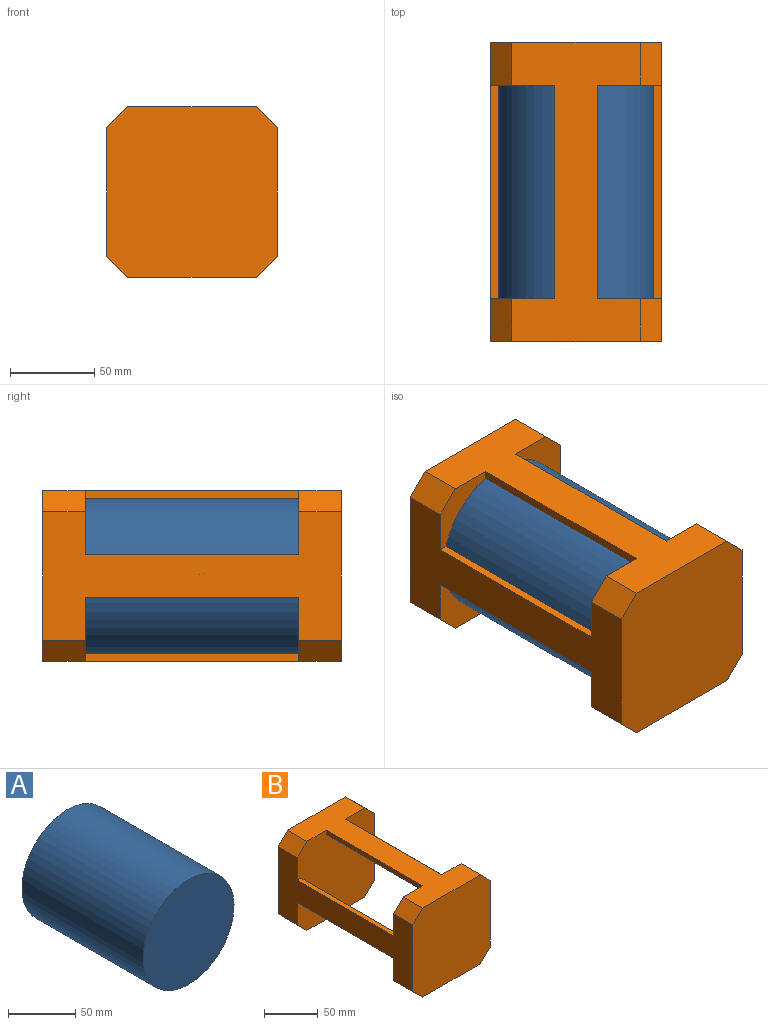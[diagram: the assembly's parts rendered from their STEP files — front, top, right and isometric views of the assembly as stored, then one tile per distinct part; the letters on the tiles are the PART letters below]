
ASSEMBLY  parts=2 mates=1
PART A: 3 faces, bbox 95.3x127x95.3 mm
  f0: cylinder r=47.62mm len=127mm, axis (0,-1,0), area 38003.1mm2, adj f1,f2
  f1: plane 95.25x95.25mm, normal (0,1,0), area 7125.6mm2, adj f0
  f2: plane 95.25x95.25mm, normal (0,-1,0), area 7125.6mm2, adj f0
PART B: 28 faces, bbox 101.6x177.8x101.6 mm
  f0: plane 101.6x101.6mm, normal (0,1,0), area 9619.4mm2, adj f1,f2,f3,f4,f5,f6,f7,f8
  f1: plane 177.8x76.2mm, normal (0,0,-1), area 7096.8mm2, adj f0,f2,f8,f9,f13,f14,f22,f23
  f2: plane 25.4x12.7mm, normal (0.71,0,-0.71), area 456.2mm2, adj f0,f1,f3,f9
  f3: plane 177.8x76.2mm, normal (1,0,0), area 7096.8mm2, adj f0,f2,f4,f9,f19,f21,f22,f23
  f4: plane 25.4x12.7mm, normal (0.71,0,0.71), area 456.2mm2, adj f0,f3,f5,f9
  f5: plane 177.8x76.2mm, normal (0,0,1), area 7096.8mm2, adj f0,f4,f6,f9,f10,f12,f22,f24
  f6: plane 25.4x12.7mm, normal (-0.71,0,0.71), area 456.2mm2, adj f0,f5,f7,f9
  f7: plane 177.8x76.2mm, normal (-1,0,0), area 7096.8mm2, adj f0,f6,f8,f9,f17,f18,f22,f25
  f8: plane 25.4x12.7mm, normal (-0.71,0,-0.71), area 456.2mm2, adj f0,f1,f7,f9
  f9: plane 101.6x101.6mm, normal (0,-1,0), area 10000mm2, adj f1,f2,f3,f4,f5,f6,f7,f8
  f10: plane 127x4.9mm, normal (-1,0,0), area 622.2mm2, adj f0,f5,f11,f22
  f11: cylinder r=47.62mm len=127mm, axis (0,-1,0), area 3265.3mm2, adj f0,f10,f12,f22
  f12: plane 127x4.9mm, normal (1,0,0), area 622.2mm2, adj f0,f5,f11,f22
  f13: plane 127x4.9mm, normal (-1,0,0), area 622.2mm2, adj f0,f1,f15,f22
  f14: plane 127x4.9mm, normal (1,0,0), area 622.2mm2, adj f0,f1,f15,f22
  f15: cylinder r=47.62mm len=127mm, axis (0,-1,0), area 3265.3mm2, adj f0,f13,f14,f22
  f16: cylinder r=47.62mm len=127mm, axis (0,-1,0), area 3265.3mm2, adj f0,f17,f18,f22
  f17: plane 127x4.9mm, normal (0,0,1), area 622.2mm2, adj f0,f7,f16,f22
  f18: plane 127x4.9mm, normal (0,0,-1), area 622.2mm2, adj f0,f7,f16,f22
  f19: plane 127x4.9mm, normal (0,0,1), area 622.2mm2, adj f0,f3,f20,f22
  f20: cylinder r=47.62mm len=127mm, axis (0,-1,0), area 3265.3mm2, adj f0,f19,f21,f22
  f21: plane 127x4.9mm, normal (0,0,-1), area 622.2mm2, adj f0,f3,f20,f22
  f22: plane 101.6x101.6mm, normal (0,-1,0), area 9619.4mm2, adj f1,f3,f5,f7,f10,f11,f12,f13
  f23: plane 25.4x12.7mm, normal (0.71,0,-0.71), area 456.2mm2, adj f1,f3,f22,f27
  f24: plane 25.4x12.7mm, normal (0.71,0,0.71), area 456.2mm2, adj f3,f5,f22,f27
  f25: plane 25.4x12.7mm, normal (-0.71,0,0.71), area 456.2mm2, adj f5,f7,f22,f27
  f26: plane 25.4x12.7mm, normal (-0.71,0,-0.71), area 456.2mm2, adj f1,f7,f22,f27
  f27: plane 101.6x101.6mm, normal (0,1,0), area 10000mm2, adj f1,f3,f5,f7,f23,f24,f25,f26
PLACE A t=(-525.14,-64.41,0.28)mm
PLACE B t=(-1.9,-64.41,0.28)mm
MATE fastened A.f0 <-> B.f20  axis (0,-1,0) through (-1.9,62.59,0.28)mm
